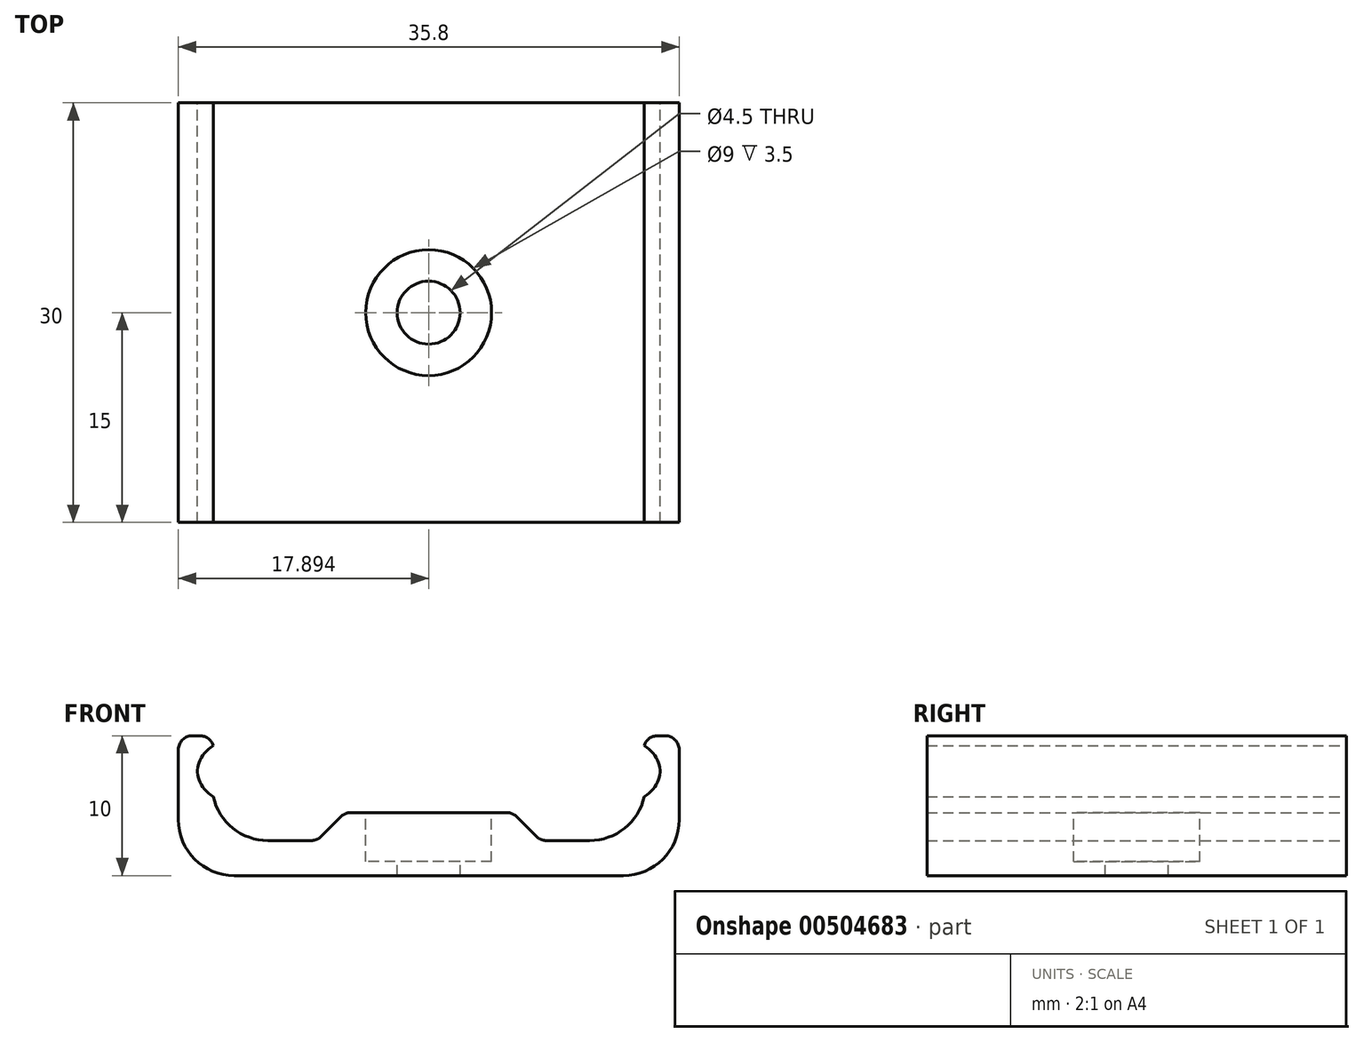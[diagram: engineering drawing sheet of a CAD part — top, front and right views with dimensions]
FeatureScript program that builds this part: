
annotation { "Feature Type Name" : "Feature", "Feature Type Description" : "" }
export const myFeature = defineFeature(function(context is Context, id is Id, definition is map)
    precondition{}
    {
        {
            var Q0;
            Q0=qCreatedBy(makeId("Front.planeOp"),FACE);
            var sketch = newSketch(context, id + "F0", { "sketchPlane" : qUnion([Q0])});
            skLineSegment(sketch, "E0", {"start": v(-17.9, 0) * mm, "end": v(17.9, 0) * mm});
            skLineSegment(sketch, "E1", {"start": v(-16.4, 15.5) * mm, "end": v(-16.4, -15.28) * mm, "construction": true});
            skLineSegment(sketch, "E2", {"start": v(16.4, 15.5) * mm, "end": v(16.4, -15.28) * mm, "construction": true});
            skLineSegment(sketch, "E3", {"start": v(15.4, 2.5) * mm, "end": v(8, 2.5) * mm});
            skLineSegment(sketch, "E4", {"start": v(0, 15.5) * mm, "end": v(0, -15.28) * mm, "construction": true});
            skLineSegment(sketch, "E5", {"start": v(-8, 2.5) * mm, "end": v(-6, 4.5) * mm});
            skLineSegment(sketch, "E6", {"start": v(-6, 4.5) * mm, "end": v(6, 4.5) * mm});
            skLineSegment(sketch, "E7", {"start": v(6, 4.5) * mm, "end": v(8, 2.5) * mm});
            skLineSegment(sketch, "E8.trimOffspring", {"start": v(-8, 2.5) * mm, "end": v(-15.4, 2.5) * mm});
            skLineSegment(sketch, "E9", {"start": v(-17.9, 10) * mm, "end": v(-15.4, 10) * mm});
            skLineSegment(sketch, "E10", {"start": v(-15.4, 10) * mm, "end": v(-15.4, 2.5) * mm});
            skLineSegment(sketch, "E11", {"start": v(17.9, 10) * mm, "end": v(15.4, 10) * mm});
            skLineSegment(sketch, "E12", {"start": v(15.4, 10) * mm, "end": v(15.4, 2.5) * mm});
            skLineSegment(sketch, "E13", {"start": v(17.9, 10) * mm, "end": v(17.9, 0) * mm});
            skLineSegment(sketch, "E14", {"start": v(-17.9, 10) * mm, "end": v(-17.9, 0) * mm});
            skEllipse(sketch, "E15", {"center": v(13.03, 7.47) * mm, "majorRadius": 3.5 * mm, "minorRadius": 2.48 * mm, "majorAxis": v(-1, 0)});
            skEllipse(sketch, "E16", {"center": v(-13.03, 7.47) * mm, "majorRadius": 3.5 * mm, "minorRadius": 2.48 * mm, "majorAxis": v(-1, 0)});
            skLineSegment(sketch, "E17", {"start": v(-19.1, 4.5) * mm, "end": v(19.4, 4.5) * mm, "construction": true});
            skSolve(sketch);
        }
        {
            var Q0;
            Q0 = qSketchRegion(id + "F0", true);
            extrude(context, id + "F1", {"entities" : qUnion([Q0]), "depth" : 30 * mm});
        }
        {
            var Q0;
            Q0=makeQuery(id+"F1.opExtrude","SWEPT_FACE",FACE,{"disambiguationData":[OSD([sQuery(id+"F0.wireOp",EDGE,"E6")])]});
            var sketch = newSketch(context, id + "F2", { "sketchPlane" : qUnion([Q0])});
            skLineSegment(sketch, "E18", {"start": v(0, -30) * mm, "end": v(0, 0) * mm, "construction": true});
            skLineSegment(sketch, "E19", {"start": v(17.95, -15) * mm, "end": v(-17.96, -15) * mm, "construction": true});
            skCircle(sketch, "E20", {"center": v(0, -15) * mm, "radius": 4 * mm});
            skSolve(sketch);
        }
        {
            var Q0;
            Q0=sQuery(id+"F2.wireOp",VERTEX,"E20.center");
            var Q1;
            Q1=makeQuery(id+"F1.opExtrude","SWEPT_BODY",BODY,{"disambiguationData":[OSD([sQuery(id+"F0.wireOp",EDGE,"E0"),sQuery(id+"F0.wireOp",EDGE,"E3"),sQuery(id+"F0.wireOp",EDGE,"E5"),sQuery(id+"F0.wireOp",EDGE,"E6"),sQuery(id+"F0.wireOp",EDGE,"E7"),sQuery(id+"F0.wireOp",EDGE,"E8.trimOffspring"),sQuery(id+"F0.wireOp",EDGE,"E9"),sQuery(id+"F0.wireOp",EDGE,"E10"),sQuery(id+"F0.wireOp",EDGE,"E11"),sQuery(id+"F0.wireOp",EDGE,"E12"),sQuery(id+"F0.wireOp",EDGE,"E13"),sQuery(id+"F0.wireOp",EDGE,"E14")])]});
            hole(context, id + "F3", {"style" : HoleStyle.C_BORE, "endStyle" : HoleEndStyle.THROUGH, "holeDiameter" : 4.5 * mm, "cBoreDiameter" : 9 * mm, "cBoreDepth" : 3.5 * mm, "isTappedThrough" : true, "tappedDepth" : 12 * mm, "tapClearance" : 3, "locations" : qUnion([Q0]), "scope" : qUnion([Q1])});
        }
        {
            var Q0;
            {var subQ0=sQuery(id+"F0.wireOp",EDGE,"E15");var subQ1=sQuery(id+"F0.wireOp",EDGE,"E12");var subQ2=makeQuery(id+"F0.imprint","INTERSECT",VERTEX,{"disambiguationData":[OD(0.0)],"derivedFrom":[subQ1,subQ0]});Q0=makeQuery(id+"F0.imprint","IMPRINT",FACE,{"disambiguationData":[TD([[makeQuery(id+"F0.imprint","IMPRINT",EDGE,{"disambiguationData":[TD([[subQ2,-1.0]])],"derivedFrom":subQ1}),-1.0]])]});}
            var Q1;
            {var subQ0=sQuery(id+"F0.wireOp",EDGE,"E15");var subQ1=sQuery(id+"F0.wireOp",EDGE,"E12");var subQ2=makeQuery(id+"F0.imprint","INTERSECT",VERTEX,{"disambiguationData":[OD(0.0)],"derivedFrom":[subQ1,subQ0]});Q1=makeQuery(id+"F0.imprint","IMPRINT",FACE,{"disambiguationData":[TD([[makeQuery(id+"F0.imprint","IMPRINT",EDGE,{"disambiguationData":[TD([[subQ2,-1.0]])],"derivedFrom":subQ1}),1.0]])]});}
            var Q2;
            {var subQ0=sQuery(id+"F0.wireOp",EDGE,"E16");var subQ1=sQuery(id+"F0.wireOp",EDGE,"E10");var subQ2=makeQuery(id+"F0.imprint","INTERSECT",VERTEX,{"disambiguationData":[OD(0.0)],"derivedFrom":[subQ1,subQ0]});Q2=makeQuery(id+"F0.imprint","IMPRINT",FACE,{"disambiguationData":[TD([[makeQuery(id+"F0.imprint","IMPRINT",EDGE,{"disambiguationData":[TD([[subQ2,-1.0]])],"derivedFrom":subQ1}),1.0]])]});}
            var Q3;
            {var subQ0=sQuery(id+"F0.wireOp",EDGE,"E16");var subQ1=sQuery(id+"F0.wireOp",EDGE,"E10");var subQ2=makeQuery(id+"F0.imprint","INTERSECT",VERTEX,{"disambiguationData":[OD(0.0)],"derivedFrom":[subQ1,subQ0]});Q3=makeQuery(id+"F0.imprint","IMPRINT",FACE,{"disambiguationData":[TD([[makeQuery(id+"F0.imprint","IMPRINT",EDGE,{"disambiguationData":[TD([[subQ2,-1.0]])],"derivedFrom":subQ1}),-1.0]])]});}
            var Q4;
            Q4=sQuery(id+"F0.wireOp",EDGE,"E15");
            extrude(context, id + "F4", {"entities" : qUnion([Q0, Q1, Q2, Q3]), "operationType" : NewBodyOperationType.REMOVE, "surfaceEntities" : qUnion([Q4]), "endBound" : BoundingType.THROUGH_ALL, "depth" : 25 * mm});
        }
        {
            var Q0;
            Q0=makeQuery(id+"F1.opExtrude","SWEPT_EDGE",EDGE,{"disambiguationData":[OSD([sQuery(id+"F0.wireOp",EDGE,"E9"),sQuery(id+"F0.wireOp",EDGE,"E14")])]});
            var Q1;
            Q1=makeQuery(id+"F1.opExtrude","SWEPT_EDGE",EDGE,{"disambiguationData":[OSD([sQuery(id+"F0.wireOp",EDGE,"E11"),sQuery(id+"F0.wireOp",EDGE,"E13")])]});
            var Q2;
            Q2=makeQuery(id+"F1.opExtrude","SWEPT_EDGE",EDGE,{"disambiguationData":[OSD([sQuery(id+"F0.wireOp",EDGE,"E9"),sQuery(id+"F0.wireOp",EDGE,"E10")])]});
            var Q3;
            Q3=makeQuery(id+"F1.opExtrude","SWEPT_EDGE",EDGE,{"disambiguationData":[OSD([sQuery(id+"F0.wireOp",EDGE,"E11"),sQuery(id+"F0.wireOp",EDGE,"E12")])]});
            var Q4;
            Q4=makeQuery(id+"F1.opExtrude","SWEPT_EDGE",EDGE,{"disambiguationData":[OSD([sQuery(id+"F0.wireOp",EDGE,"E5"),sQuery(id+"F0.wireOp",EDGE,"E8.trimOffspring")])]});
            var Q5;
            Q5=makeQuery(id+"F1.opExtrude","SWEPT_EDGE",EDGE,{"disambiguationData":[OSD([sQuery(id+"F0.wireOp",EDGE,"E6"),sQuery(id+"F0.wireOp",EDGE,"E7")])]});
            var Q6;
            Q6=makeQuery(id+"F1.opExtrude","SWEPT_EDGE",EDGE,{"disambiguationData":[OSD([sQuery(id+"F0.wireOp",EDGE,"E5"),sQuery(id+"F0.wireOp",EDGE,"E6")])]});
            var Q7;
            Q7=makeQuery(id+"F1.opExtrude","SWEPT_EDGE",EDGE,{"disambiguationData":[OSD([sQuery(id+"F0.wireOp",EDGE,"E3"),sQuery(id+"F0.wireOp",EDGE,"E7")])]});
            fillet(context, id + "F5", {"entities" : qUnion([Q0, Q1, Q2, Q3, Q4, Q5, Q6, Q7]), "radius" : 1 * mm, "tangentPropagation" : true, "allowEdgeOverflow" : false});
        }
        {
            var Q0;
            Q0=makeQuery(id+"F1.opExtrude","SWEPT_EDGE",EDGE,{"disambiguationData":[OSD([sQuery(id+"F0.wireOp",EDGE,"E8.trimOffspring"),sQuery(id+"F0.wireOp",EDGE,"E10")])]});
            var Q1;
            Q1=makeQuery(id+"F1.opExtrude","SWEPT_EDGE",EDGE,{"disambiguationData":[OSD([sQuery(id+"F0.wireOp",EDGE,"E3"),sQuery(id+"F0.wireOp",EDGE,"E12")])]});
            var Q2;
            Q2=makeQuery(id+"F1.opExtrude","SWEPT_EDGE",EDGE,{"disambiguationData":[OSD([sQuery(id+"F0.wireOp",EDGE,"E0"),sQuery(id+"F0.wireOp",EDGE,"E13")])]});
            var Q3;
            Q3=makeQuery(id+"F1.opExtrude","SWEPT_EDGE",EDGE,{"disambiguationData":[OSD([sQuery(id+"F0.wireOp",EDGE,"E0"),sQuery(id+"F0.wireOp",EDGE,"E14")])]});
            fillet(context, id + "F6", {"entities" : qUnion([Q0, Q1, Q2, Q3]), "radius" : 4 * mm, "tangentPropagation" : true, "allowEdgeOverflow" : false});
        }
    });
